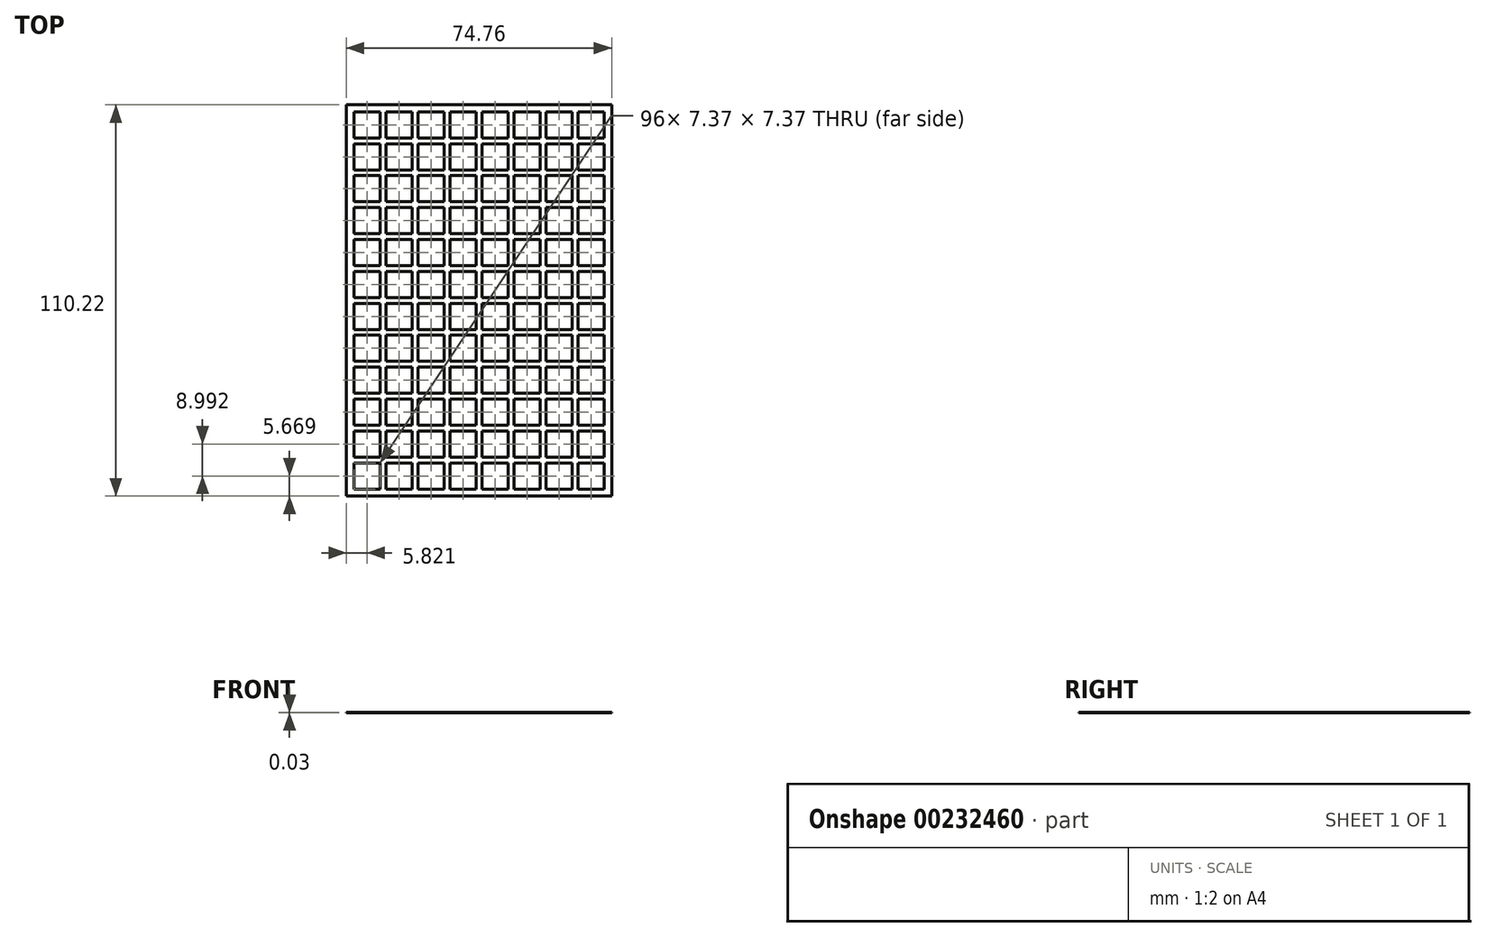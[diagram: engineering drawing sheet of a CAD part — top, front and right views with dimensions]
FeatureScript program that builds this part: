
annotation { "Feature Type Name" : "Feature", "Feature Type Description" : "" }
export const myFeature = defineFeature(function(context is Context, id is Id, definition is map)
    precondition{}
    {
        {
            var Q0;
            Q0=qCreatedBy(makeId("Top.planeOp"),FACE);
            var sketch = newSketch(context, id + "F0", { "sketchPlane" : qUnion([Q0])});
            skLineSegment(sketch, "E0.bottom", {"start": v(-37.38, 55.1) * mm, "end": v(37.38, 55.1) * mm});
            skLineSegment(sketch, "E0.top", {"start": v(-37.38, -55.1) * mm, "end": v(37.38, -55.1) * mm});
            skLineSegment(sketch, "E0.left", {"start": v(-37.38, 55.1) * mm, "end": v(-37.38, -55.1) * mm});
            skLineSegment(sketch, "E0.right", {"start": v(37.38, 55.1) * mm, "end": v(37.38, -55.1) * mm});
            skLineSegment(sketch, "E1.bottom", {"start": v(-35.24, 53.15) * mm, "end": v(-27.88, 53.15) * mm});
            skLineSegment(sketch, "E1.top", {"start": v(-35.24, 45.78) * mm, "end": v(-27.88, 45.78) * mm});
            skLineSegment(sketch, "E1.left", {"start": v(-35.24, 53.15) * mm, "end": v(-35.24, 45.78) * mm});
            skLineSegment(sketch, "E1.right", {"start": v(-27.88, 53.15) * mm, "end": v(-27.88, 45.78) * mm});
            skLineSegment(sketch, "E2.1.0.0", {"start": v(-18.86, 53.15) * mm, "end": v(-18.86, 45.78) * mm});
            skLineSegment(sketch, "E2.1.0.1", {"start": v(-26.23, 45.78) * mm, "end": v(-18.86, 45.78) * mm});
            skLineSegment(sketch, "E2.1.0.2", {"start": v(-26.23, 53.15) * mm, "end": v(-26.23, 45.78) * mm});
            skLineSegment(sketch, "E2.1.0.3", {"start": v(-26.23, 53.15) * mm, "end": v(-18.86, 53.15) * mm});
            skLineSegment(sketch, "E2.2.0.0", {"start": v(-9.84, 53.15) * mm, "end": v(-9.84, 45.78) * mm});
            skLineSegment(sketch, "E2.2.0.1", {"start": v(-17.2, 45.78) * mm, "end": v(-9.84, 45.78) * mm});
            skLineSegment(sketch, "E2.2.0.2", {"start": v(-17.2, 53.15) * mm, "end": v(-17.2, 45.78) * mm});
            skLineSegment(sketch, "E2.2.0.3", {"start": v(-17.2, 53.15) * mm, "end": v(-9.84, 53.15) * mm});
            skLineSegment(sketch, "E3.1.0.0", {"start": v(0.83, 53.15) * mm, "end": v(0.83, 45.78) * mm});
            skLineSegment(sketch, "E3.1.0.1", {"start": v(0.83, 45.78) * mm, "end": v(8.2, 45.78) * mm});
            skLineSegment(sketch, "E3.1.0.2", {"start": v(-0.83, 53.15) * mm, "end": v(-0.83, 45.78) * mm});
            skLineSegment(sketch, "E3.1.0.3", {"start": v(0.83, 53.15) * mm, "end": v(8.2, 53.15) * mm});
            skLineSegment(sketch, "E3.1.0.4", {"start": v(17.2, 53.15) * mm, "end": v(17.2, 45.78) * mm});
            skLineSegment(sketch, "E3.1.0.5", {"start": v(-8.2, 53.15) * mm, "end": v(-8.2, 45.78) * mm});
            skLineSegment(sketch, "E3.1.0.6", {"start": v(-8.2, 45.78) * mm, "end": v(-0.83, 45.78) * mm});
            skLineSegment(sketch, "E3.1.0.7", {"start": v(9.84, 53.15) * mm, "end": v(17.2, 53.15) * mm});
            skLineSegment(sketch, "E3.1.0.8", {"start": v(9.84, 45.78) * mm, "end": v(17.2, 45.78) * mm});
            skLineSegment(sketch, "E3.1.0.9", {"start": v(8.2, 53.15) * mm, "end": v(8.2, 45.78) * mm});
            skLineSegment(sketch, "E3.1.0.10", {"start": v(-8.2, 53.15) * mm, "end": v(-0.83, 53.15) * mm});
            skLineSegment(sketch, "E3.1.0.11", {"start": v(9.84, 53.15) * mm, "end": v(9.84, 45.78) * mm});
            skLineSegment(sketch, "E3.2.0.0", {"start": v(27.88, 53.15) * mm, "end": v(27.88, 45.78) * mm});
            skLineSegment(sketch, "E3.2.0.1", {"start": v(27.88, 45.78) * mm, "end": v(35.24, 45.78) * mm});
            skLineSegment(sketch, "E3.2.0.2", {"start": v(26.23, 53.15) * mm, "end": v(26.23, 45.78) * mm});
            skLineSegment(sketch, "E3.2.0.3", {"start": v(27.88, 53.15) * mm, "end": v(35.24, 53.15) * mm});
            skLineSegment(sketch, "E3.2.0.5", {"start": v(18.86, 53.15) * mm, "end": v(18.86, 45.78) * mm});
            skLineSegment(sketch, "E3.2.0.6", {"start": v(18.86, 45.78) * mm, "end": v(26.23, 45.78) * mm});
            skLineSegment(sketch, "E3.2.0.9", {"start": v(35.24, 53.15) * mm, "end": v(35.24, 45.78) * mm});
            skLineSegment(sketch, "E3.2.0.10", {"start": v(18.86, 53.15) * mm, "end": v(26.23, 53.15) * mm});
            skLineSegment(sketch, "E4.1.0.0", {"start": v(-8.2, 44.16) * mm, "end": v(-0.83, 44.16) * mm});
            skLineSegment(sketch, "E4.1.0.1", {"start": v(0.83, 44.16) * mm, "end": v(8.2, 44.16) * mm});
            skLineSegment(sketch, "E4.1.0.2", {"start": v(18.86, 44.16) * mm, "end": v(26.23, 44.16) * mm});
            skLineSegment(sketch, "E4.1.0.3", {"start": v(-17.2, 36.8) * mm, "end": v(-9.84, 36.8) * mm});
            skLineSegment(sketch, "E4.1.0.4", {"start": v(8.2, 44.16) * mm, "end": v(8.2, 36.8) * mm});
            skLineSegment(sketch, "E4.1.0.5", {"start": v(-35.24, 36.8) * mm, "end": v(-27.88, 36.8) * mm});
            skLineSegment(sketch, "E4.1.0.6", {"start": v(-17.2, 44.16) * mm, "end": v(-17.2, 36.8) * mm});
            skLineSegment(sketch, "E4.1.0.7", {"start": v(-17.2, 44.16) * mm, "end": v(-9.84, 44.16) * mm});
            skLineSegment(sketch, "E4.1.0.8", {"start": v(-0.83, 44.16) * mm, "end": v(-0.83, 36.8) * mm});
            skLineSegment(sketch, "E4.1.0.9", {"start": v(-35.24, 44.16) * mm, "end": v(-27.88, 44.16) * mm});
            skLineSegment(sketch, "E4.1.0.10", {"start": v(27.88, 44.16) * mm, "end": v(35.24, 44.16) * mm});
            skLineSegment(sketch, "E4.1.0.11", {"start": v(-8.2, 36.8) * mm, "end": v(-0.83, 36.8) * mm});
            skLineSegment(sketch, "E4.1.0.12", {"start": v(-35.24, 44.16) * mm, "end": v(-35.24, 36.8) * mm});
            skLineSegment(sketch, "E4.1.0.13", {"start": v(-27.88, 44.16) * mm, "end": v(-27.88, 36.8) * mm});
            skLineSegment(sketch, "E4.1.0.14", {"start": v(0.83, 36.8) * mm, "end": v(8.2, 36.8) * mm});
            skLineSegment(sketch, "E4.1.0.15", {"start": v(18.86, 36.8) * mm, "end": v(26.23, 36.8) * mm});
            skLineSegment(sketch, "E4.1.0.16", {"start": v(-18.86, 44.16) * mm, "end": v(-18.86, 36.8) * mm});
            skLineSegment(sketch, "E4.1.0.17", {"start": v(-26.23, 36.8) * mm, "end": v(-18.86, 36.8) * mm});
            skLineSegment(sketch, "E4.1.0.18", {"start": v(-26.23, 44.16) * mm, "end": v(-26.23, 36.8) * mm});
            skLineSegment(sketch, "E4.1.0.19", {"start": v(-26.23, 44.16) * mm, "end": v(-18.86, 44.16) * mm});
            skLineSegment(sketch, "E4.1.0.20", {"start": v(-9.84, 44.16) * mm, "end": v(-9.84, 36.8) * mm});
            skLineSegment(sketch, "E4.1.0.21", {"start": v(9.84, 44.16) * mm, "end": v(9.84, 36.8) * mm});
            skLineSegment(sketch, "E4.1.0.22", {"start": v(9.84, 44.16) * mm, "end": v(17.2, 44.16) * mm});
            skLineSegment(sketch, "E4.1.0.23", {"start": v(17.2, 44.16) * mm, "end": v(17.2, 36.8) * mm});
            skLineSegment(sketch, "E4.1.0.24", {"start": v(27.88, 36.8) * mm, "end": v(35.24, 36.8) * mm});
            skLineSegment(sketch, "E4.1.0.25", {"start": v(0.83, 44.16) * mm, "end": v(0.83, 36.8) * mm});
            skLineSegment(sketch, "E4.1.0.26", {"start": v(18.86, 44.16) * mm, "end": v(18.86, 36.8) * mm});
            skLineSegment(sketch, "E4.1.0.27", {"start": v(27.88, 44.16) * mm, "end": v(27.88, 36.8) * mm});
            skLineSegment(sketch, "E4.1.0.28", {"start": v(9.84, 36.8) * mm, "end": v(17.2, 36.8) * mm});
            skLineSegment(sketch, "E4.1.0.29", {"start": v(26.23, 44.16) * mm, "end": v(26.23, 36.8) * mm});
            skLineSegment(sketch, "E4.1.0.30", {"start": v(-8.2, 44.16) * mm, "end": v(-8.2, 36.8) * mm});
            skLineSegment(sketch, "E4.1.0.31", {"start": v(35.24, 44.16) * mm, "end": v(35.24, 36.8) * mm});
            skLineSegment(sketch, "E4.2.0.0", {"start": v(-8.2, 35.17) * mm, "end": v(-0.83, 35.17) * mm});
            skLineSegment(sketch, "E4.2.0.1", {"start": v(0.83, 35.17) * mm, "end": v(8.2, 35.17) * mm});
            skLineSegment(sketch, "E4.2.0.2", {"start": v(18.86, 35.17) * mm, "end": v(26.23, 35.17) * mm});
            skLineSegment(sketch, "E4.2.0.3", {"start": v(-17.2, 27.8) * mm, "end": v(-9.84, 27.8) * mm});
            skLineSegment(sketch, "E4.2.0.4", {"start": v(8.2, 35.17) * mm, "end": v(8.2, 27.8) * mm});
            skLineSegment(sketch, "E4.2.0.5", {"start": v(-35.24, 27.8) * mm, "end": v(-27.88, 27.8) * mm});
            skLineSegment(sketch, "E4.2.0.6", {"start": v(-17.2, 35.17) * mm, "end": v(-17.2, 27.8) * mm});
            skLineSegment(sketch, "E4.2.0.7", {"start": v(-17.2, 35.17) * mm, "end": v(-9.84, 35.17) * mm});
            skLineSegment(sketch, "E4.2.0.8", {"start": v(-0.83, 35.17) * mm, "end": v(-0.83, 27.8) * mm});
            skLineSegment(sketch, "E4.2.0.9", {"start": v(-35.24, 35.17) * mm, "end": v(-27.88, 35.17) * mm});
            skLineSegment(sketch, "E4.2.0.10", {"start": v(27.88, 35.17) * mm, "end": v(35.24, 35.17) * mm});
            skLineSegment(sketch, "E4.2.0.11", {"start": v(-8.2, 27.8) * mm, "end": v(-0.83, 27.8) * mm});
            skLineSegment(sketch, "E4.2.0.12", {"start": v(-35.24, 35.17) * mm, "end": v(-35.24, 27.8) * mm});
            skLineSegment(sketch, "E4.2.0.13", {"start": v(-27.88, 35.17) * mm, "end": v(-27.88, 27.8) * mm});
            skLineSegment(sketch, "E4.2.0.14", {"start": v(0.83, 27.8) * mm, "end": v(8.2, 27.8) * mm});
            skLineSegment(sketch, "E4.2.0.15", {"start": v(18.86, 27.8) * mm, "end": v(26.23, 27.8) * mm});
            skLineSegment(sketch, "E4.2.0.16", {"start": v(-18.86, 35.17) * mm, "end": v(-18.86, 27.8) * mm});
            skLineSegment(sketch, "E4.2.0.17", {"start": v(-26.23, 27.8) * mm, "end": v(-18.86, 27.8) * mm});
            skLineSegment(sketch, "E4.2.0.18", {"start": v(-26.23, 35.17) * mm, "end": v(-26.23, 27.8) * mm});
            skLineSegment(sketch, "E4.2.0.19", {"start": v(-26.23, 35.17) * mm, "end": v(-18.86, 35.17) * mm});
            skLineSegment(sketch, "E4.2.0.20", {"start": v(-9.84, 35.17) * mm, "end": v(-9.84, 27.8) * mm});
            skLineSegment(sketch, "E4.2.0.21", {"start": v(9.84, 35.17) * mm, "end": v(9.84, 27.8) * mm});
            skLineSegment(sketch, "E4.2.0.22", {"start": v(9.84, 35.17) * mm, "end": v(17.2, 35.17) * mm});
            skLineSegment(sketch, "E4.2.0.23", {"start": v(17.2, 35.17) * mm, "end": v(17.2, 27.8) * mm});
            skLineSegment(sketch, "E4.2.0.24", {"start": v(27.88, 27.8) * mm, "end": v(35.24, 27.8) * mm});
            skLineSegment(sketch, "E4.2.0.25", {"start": v(0.83, 35.17) * mm, "end": v(0.83, 27.8) * mm});
            skLineSegment(sketch, "E4.2.0.26", {"start": v(18.86, 35.17) * mm, "end": v(18.86, 27.8) * mm});
            skLineSegment(sketch, "E4.2.0.27", {"start": v(27.88, 35.17) * mm, "end": v(27.88, 27.8) * mm});
            skLineSegment(sketch, "E4.2.0.28", {"start": v(9.84, 27.8) * mm, "end": v(17.2, 27.8) * mm});
            skLineSegment(sketch, "E4.2.0.29", {"start": v(26.23, 35.17) * mm, "end": v(26.23, 27.8) * mm});
            skLineSegment(sketch, "E4.2.0.30", {"start": v(-8.2, 35.17) * mm, "end": v(-8.2, 27.8) * mm});
            skLineSegment(sketch, "E4.2.0.31", {"start": v(35.24, 35.17) * mm, "end": v(35.24, 27.8) * mm});
            skLineSegment(sketch, "E4.direction1", {"start": v(-35.24, 45.78) * mm, "end": v(-35.24, 36.8) * mm, "construction": true});
            skLineSegment(sketch, "E5.0.3.0", {"start": v(-8.2, 26.17) * mm, "end": v(-0.83, 26.17) * mm});
            skLineSegment(sketch, "E5.3.3.0", {"start": v(0.83, 26.17) * mm, "end": v(8.2, 26.17) * mm});
            skLineSegment(sketch, "E5.6.3.0", {"start": v(18.86, 26.17) * mm, "end": v(26.23, 26.17) * mm});
            skLineSegment(sketch, "E5.9.3.0", {"start": v(-17.2, 18.8) * mm, "end": v(-9.84, 18.8) * mm});
            skLineSegment(sketch, "E5.12.3.0", {"start": v(8.2, 26.17) * mm, "end": v(8.2, 18.8) * mm});
            skLineSegment(sketch, "E5.15.3.0", {"start": v(-35.24, 18.8) * mm, "end": v(-27.88, 18.8) * mm});
            skLineSegment(sketch, "E5.18.3.0", {"start": v(-17.2, 26.17) * mm, "end": v(-17.2, 18.8) * mm});
            skLineSegment(sketch, "E5.21.3.0", {"start": v(-17.2, 26.17) * mm, "end": v(-9.84, 26.17) * mm});
            skLineSegment(sketch, "E5.24.3.0", {"start": v(-0.83, 26.17) * mm, "end": v(-0.83, 18.8) * mm});
            skLineSegment(sketch, "E5.27.3.0", {"start": v(-35.24, 26.17) * mm, "end": v(-27.88, 26.17) * mm});
            skLineSegment(sketch, "E5.30.3.0", {"start": v(27.88, 26.17) * mm, "end": v(35.24, 26.17) * mm});
            skLineSegment(sketch, "E5.33.3.0", {"start": v(-8.2, 18.8) * mm, "end": v(-0.83, 18.8) * mm});
            skLineSegment(sketch, "E5.36.3.0", {"start": v(-35.24, 26.17) * mm, "end": v(-35.24, 18.8) * mm});
            skLineSegment(sketch, "E5.39.3.0", {"start": v(-27.88, 26.17) * mm, "end": v(-27.88, 18.8) * mm});
            skLineSegment(sketch, "E5.42.3.0", {"start": v(0.83, 18.8) * mm, "end": v(8.2, 18.8) * mm});
            skLineSegment(sketch, "E5.45.3.0", {"start": v(18.86, 18.8) * mm, "end": v(26.23, 18.8) * mm});
            skLineSegment(sketch, "E5.48.3.0", {"start": v(-18.86, 26.17) * mm, "end": v(-18.86, 18.8) * mm});
            skLineSegment(sketch, "E5.51.3.0", {"start": v(-26.23, 18.8) * mm, "end": v(-18.86, 18.8) * mm});
            skLineSegment(sketch, "E5.54.3.0", {"start": v(-26.23, 26.17) * mm, "end": v(-26.23, 18.8) * mm});
            skLineSegment(sketch, "E5.57.3.0", {"start": v(-26.23, 26.17) * mm, "end": v(-18.86, 26.17) * mm});
            skLineSegment(sketch, "E5.60.3.0", {"start": v(-9.84, 26.17) * mm, "end": v(-9.84, 18.8) * mm});
            skLineSegment(sketch, "E5.63.3.0", {"start": v(9.84, 26.17) * mm, "end": v(9.84, 18.8) * mm});
            skLineSegment(sketch, "E5.66.3.0", {"start": v(9.84, 26.17) * mm, "end": v(17.2, 26.17) * mm});
            skLineSegment(sketch, "E5.69.3.0", {"start": v(17.2, 26.17) * mm, "end": v(17.2, 18.8) * mm});
            skLineSegment(sketch, "E5.72.3.0", {"start": v(27.88, 18.8) * mm, "end": v(35.24, 18.8) * mm});
            skLineSegment(sketch, "E5.75.3.0", {"start": v(0.83, 26.17) * mm, "end": v(0.83, 18.8) * mm});
            skLineSegment(sketch, "E5.78.3.0", {"start": v(18.86, 26.17) * mm, "end": v(18.86, 18.8) * mm});
            skLineSegment(sketch, "E5.81.3.0", {"start": v(27.88, 26.17) * mm, "end": v(27.88, 18.8) * mm});
            skLineSegment(sketch, "E5.84.3.0", {"start": v(9.84, 18.8) * mm, "end": v(17.2, 18.8) * mm});
            skLineSegment(sketch, "E5.87.3.0", {"start": v(26.23, 26.17) * mm, "end": v(26.23, 18.8) * mm});
            skLineSegment(sketch, "E5.90.3.0", {"start": v(-8.2, 26.17) * mm, "end": v(-8.2, 18.8) * mm});
            skLineSegment(sketch, "E5.93.3.0", {"start": v(35.24, 26.17) * mm, "end": v(35.24, 18.8) * mm});
            skLineSegment(sketch, "E5.0.4.0", {"start": v(-8.2, 17.18) * mm, "end": v(-0.83, 17.18) * mm});
            skLineSegment(sketch, "E5.3.4.0", {"start": v(0.83, 17.18) * mm, "end": v(8.2, 17.18) * mm});
            skLineSegment(sketch, "E5.6.4.0", {"start": v(18.86, 17.18) * mm, "end": v(26.23, 17.18) * mm});
            skLineSegment(sketch, "E5.9.4.0", {"start": v(-17.2, 9.82) * mm, "end": v(-9.84, 9.82) * mm});
            skLineSegment(sketch, "E5.12.4.0", {"start": v(8.2, 17.18) * mm, "end": v(8.2, 9.82) * mm});
            skLineSegment(sketch, "E5.15.4.0", {"start": v(-35.24, 9.82) * mm, "end": v(-27.88, 9.82) * mm});
            skLineSegment(sketch, "E5.18.4.0", {"start": v(-17.2, 17.18) * mm, "end": v(-17.2, 9.82) * mm});
            skLineSegment(sketch, "E5.21.4.0", {"start": v(-17.2, 17.18) * mm, "end": v(-9.84, 17.18) * mm});
            skLineSegment(sketch, "E5.24.4.0", {"start": v(-0.83, 17.18) * mm, "end": v(-0.83, 9.82) * mm});
            skLineSegment(sketch, "E5.27.4.0", {"start": v(-35.24, 17.18) * mm, "end": v(-27.88, 17.18) * mm});
            skLineSegment(sketch, "E5.30.4.0", {"start": v(27.88, 17.18) * mm, "end": v(35.24, 17.18) * mm});
            skLineSegment(sketch, "E5.33.4.0", {"start": v(-8.2, 9.82) * mm, "end": v(-0.83, 9.82) * mm});
            skLineSegment(sketch, "E5.36.4.0", {"start": v(-35.24, 17.18) * mm, "end": v(-35.24, 9.82) * mm});
            skLineSegment(sketch, "E5.39.4.0", {"start": v(-27.88, 17.18) * mm, "end": v(-27.88, 9.82) * mm});
            skLineSegment(sketch, "E5.42.4.0", {"start": v(0.83, 9.82) * mm, "end": v(8.2, 9.82) * mm});
            skLineSegment(sketch, "E5.45.4.0", {"start": v(18.86, 9.82) * mm, "end": v(26.23, 9.82) * mm});
            skLineSegment(sketch, "E5.48.4.0", {"start": v(-18.86, 17.18) * mm, "end": v(-18.86, 9.82) * mm});
            skLineSegment(sketch, "E5.51.4.0", {"start": v(-26.23, 9.82) * mm, "end": v(-18.86, 9.82) * mm});
            skLineSegment(sketch, "E5.54.4.0", {"start": v(-26.23, 17.18) * mm, "end": v(-26.23, 9.82) * mm});
            skLineSegment(sketch, "E5.57.4.0", {"start": v(-26.23, 17.18) * mm, "end": v(-18.86, 17.18) * mm});
            skLineSegment(sketch, "E5.60.4.0", {"start": v(-9.84, 17.18) * mm, "end": v(-9.84, 9.82) * mm});
            skLineSegment(sketch, "E5.63.4.0", {"start": v(9.84, 17.18) * mm, "end": v(9.84, 9.82) * mm});
            skLineSegment(sketch, "E5.66.4.0", {"start": v(9.84, 17.18) * mm, "end": v(17.2, 17.18) * mm});
            skLineSegment(sketch, "E5.69.4.0", {"start": v(17.2, 17.18) * mm, "end": v(17.2, 9.82) * mm});
            skLineSegment(sketch, "E5.72.4.0", {"start": v(27.88, 9.82) * mm, "end": v(35.24, 9.82) * mm});
            skLineSegment(sketch, "E5.75.4.0", {"start": v(0.83, 17.18) * mm, "end": v(0.83, 9.82) * mm});
            skLineSegment(sketch, "E5.78.4.0", {"start": v(18.86, 17.18) * mm, "end": v(18.86, 9.82) * mm});
            skLineSegment(sketch, "E5.81.4.0", {"start": v(27.88, 17.18) * mm, "end": v(27.88, 9.82) * mm});
            skLineSegment(sketch, "E5.84.4.0", {"start": v(9.84, 9.82) * mm, "end": v(17.2, 9.82) * mm});
            skLineSegment(sketch, "E5.87.4.0", {"start": v(26.23, 17.18) * mm, "end": v(26.23, 9.82) * mm});
            skLineSegment(sketch, "E5.90.4.0", {"start": v(-8.2, 17.18) * mm, "end": v(-8.2, 9.82) * mm});
            skLineSegment(sketch, "E5.93.4.0", {"start": v(35.24, 17.18) * mm, "end": v(35.24, 9.82) * mm});
            skLineSegment(sketch, "E5.0.5.0", {"start": v(-8.2, 8.2) * mm, "end": v(-0.83, 8.2) * mm});
            skLineSegment(sketch, "E5.3.5.0", {"start": v(0.83, 8.2) * mm, "end": v(8.2, 8.2) * mm});
            skLineSegment(sketch, "E5.6.5.0", {"start": v(18.86, 8.2) * mm, "end": v(26.23, 8.2) * mm});
            skLineSegment(sketch, "E5.9.5.0", {"start": v(-17.2, 0.83) * mm, "end": v(-9.84, 0.83) * mm});
            skLineSegment(sketch, "E5.12.5.0", {"start": v(8.2, 8.2) * mm, "end": v(8.2, 0.83) * mm});
            skLineSegment(sketch, "E5.15.5.0", {"start": v(-35.24, 0.83) * mm, "end": v(-27.88, 0.83) * mm});
            skLineSegment(sketch, "E5.18.5.0", {"start": v(-17.2, 8.2) * mm, "end": v(-17.2, 0.83) * mm});
            skLineSegment(sketch, "E5.21.5.0", {"start": v(-17.2, 8.2) * mm, "end": v(-9.84, 8.2) * mm});
            skLineSegment(sketch, "E5.24.5.0", {"start": v(-0.83, 8.2) * mm, "end": v(-0.83, 0.83) * mm});
            skLineSegment(sketch, "E5.27.5.0", {"start": v(-35.24, 8.2) * mm, "end": v(-27.88, 8.2) * mm});
            skLineSegment(sketch, "E5.30.5.0", {"start": v(27.88, 8.2) * mm, "end": v(35.24, 8.2) * mm});
            skLineSegment(sketch, "E5.33.5.0", {"start": v(-8.2, 0.83) * mm, "end": v(-0.83, 0.83) * mm});
            skLineSegment(sketch, "E5.36.5.0", {"start": v(-35.24, 8.2) * mm, "end": v(-35.24, 0.83) * mm});
            skLineSegment(sketch, "E5.39.5.0", {"start": v(-27.88, 8.2) * mm, "end": v(-27.88, 0.83) * mm});
            skLineSegment(sketch, "E5.42.5.0", {"start": v(0.83, 0.83) * mm, "end": v(8.2, 0.83) * mm});
            skLineSegment(sketch, "E5.45.5.0", {"start": v(18.86, 0.83) * mm, "end": v(26.23, 0.83) * mm});
            skLineSegment(sketch, "E5.48.5.0", {"start": v(-18.86, 8.2) * mm, "end": v(-18.86, 0.83) * mm});
            skLineSegment(sketch, "E5.51.5.0", {"start": v(-26.23, 0.83) * mm, "end": v(-18.86, 0.83) * mm});
            skLineSegment(sketch, "E5.54.5.0", {"start": v(-26.23, 8.2) * mm, "end": v(-26.23, 0.83) * mm});
            skLineSegment(sketch, "E5.57.5.0", {"start": v(-26.23, 8.2) * mm, "end": v(-18.86, 8.2) * mm});
            skLineSegment(sketch, "E5.60.5.0", {"start": v(-9.84, 8.2) * mm, "end": v(-9.84, 0.83) * mm});
            skLineSegment(sketch, "E5.63.5.0", {"start": v(9.84, 8.2) * mm, "end": v(9.84, 0.83) * mm});
            skLineSegment(sketch, "E5.66.5.0", {"start": v(9.84, 8.2) * mm, "end": v(17.2, 8.2) * mm});
            skLineSegment(sketch, "E5.69.5.0", {"start": v(17.2, 8.2) * mm, "end": v(17.2, 0.83) * mm});
            skLineSegment(sketch, "E5.72.5.0", {"start": v(27.88, 0.83) * mm, "end": v(35.24, 0.83) * mm});
            skLineSegment(sketch, "E5.75.5.0", {"start": v(0.83, 8.2) * mm, "end": v(0.83, 0.83) * mm});
            skLineSegment(sketch, "E5.78.5.0", {"start": v(18.86, 8.2) * mm, "end": v(18.86, 0.83) * mm});
            skLineSegment(sketch, "E5.81.5.0", {"start": v(27.88, 8.2) * mm, "end": v(27.88, 0.83) * mm});
            skLineSegment(sketch, "E5.84.5.0", {"start": v(9.84, 0.83) * mm, "end": v(17.2, 0.83) * mm});
            skLineSegment(sketch, "E5.87.5.0", {"start": v(26.23, 8.2) * mm, "end": v(26.23, 0.83) * mm});
            skLineSegment(sketch, "E5.90.5.0", {"start": v(-8.2, 8.2) * mm, "end": v(-8.2, 0.83) * mm});
            skLineSegment(sketch, "E5.93.5.0", {"start": v(35.24, 8.2) * mm, "end": v(35.24, 0.83) * mm});
            skLineSegment(sketch, "E5.0.6.0", {"start": v(-8.2, -0.8) * mm, "end": v(-0.83, -0.8) * mm});
            skLineSegment(sketch, "E5.3.6.0", {"start": v(0.83, -0.8) * mm, "end": v(8.2, -0.8) * mm});
            skLineSegment(sketch, "E5.6.6.0", {"start": v(18.86, -0.8) * mm, "end": v(26.23, -0.8) * mm});
            skLineSegment(sketch, "E5.9.6.0", {"start": v(-17.2, -8.17) * mm, "end": v(-9.84, -8.17) * mm});
            skLineSegment(sketch, "E5.12.6.0", {"start": v(8.2, -0.8) * mm, "end": v(8.2, -8.17) * mm});
            skLineSegment(sketch, "E5.15.6.0", {"start": v(-35.24, -8.17) * mm, "end": v(-27.88, -8.17) * mm});
            skLineSegment(sketch, "E5.18.6.0", {"start": v(-17.2, -0.8) * mm, "end": v(-17.2, -8.17) * mm});
            skLineSegment(sketch, "E5.21.6.0", {"start": v(-17.2, -0.8) * mm, "end": v(-9.84, -0.8) * mm});
            skLineSegment(sketch, "E5.24.6.0", {"start": v(-0.83, -0.8) * mm, "end": v(-0.83, -8.17) * mm});
            skLineSegment(sketch, "E5.27.6.0", {"start": v(-35.24, -0.8) * mm, "end": v(-27.88, -0.8) * mm});
            skLineSegment(sketch, "E5.30.6.0", {"start": v(27.88, -0.8) * mm, "end": v(35.24, -0.8) * mm});
            skLineSegment(sketch, "E5.33.6.0", {"start": v(-8.2, -8.17) * mm, "end": v(-0.83, -8.17) * mm});
            skLineSegment(sketch, "E5.36.6.0", {"start": v(-35.24, -0.8) * mm, "end": v(-35.24, -8.17) * mm});
            skLineSegment(sketch, "E5.39.6.0", {"start": v(-27.88, -0.8) * mm, "end": v(-27.88, -8.17) * mm});
            skLineSegment(sketch, "E5.42.6.0", {"start": v(0.83, -8.17) * mm, "end": v(8.2, -8.17) * mm});
            skLineSegment(sketch, "E5.45.6.0", {"start": v(18.86, -8.17) * mm, "end": v(26.23, -8.17) * mm});
            skLineSegment(sketch, "E5.48.6.0", {"start": v(-18.86, -0.8) * mm, "end": v(-18.86, -8.17) * mm});
            skLineSegment(sketch, "E5.51.6.0", {"start": v(-26.23, -8.17) * mm, "end": v(-18.86, -8.17) * mm});
            skLineSegment(sketch, "E5.54.6.0", {"start": v(-26.23, -0.8) * mm, "end": v(-26.23, -8.17) * mm});
            skLineSegment(sketch, "E5.57.6.0", {"start": v(-26.23, -0.8) * mm, "end": v(-18.86, -0.8) * mm});
            skLineSegment(sketch, "E5.60.6.0", {"start": v(-9.84, -0.8) * mm, "end": v(-9.84, -8.17) * mm});
            skLineSegment(sketch, "E5.63.6.0", {"start": v(9.84, -0.8) * mm, "end": v(9.84, -8.17) * mm});
            skLineSegment(sketch, "E5.66.6.0", {"start": v(9.84, -0.8) * mm, "end": v(17.2, -0.8) * mm});
            skLineSegment(sketch, "E5.69.6.0", {"start": v(17.2, -0.8) * mm, "end": v(17.2, -8.17) * mm});
            skLineSegment(sketch, "E5.72.6.0", {"start": v(27.88, -8.17) * mm, "end": v(35.24, -8.17) * mm});
            skLineSegment(sketch, "E5.75.6.0", {"start": v(0.83, -0.8) * mm, "end": v(0.83, -8.17) * mm});
            skLineSegment(sketch, "E5.78.6.0", {"start": v(18.86, -0.8) * mm, "end": v(18.86, -8.17) * mm});
            skLineSegment(sketch, "E5.81.6.0", {"start": v(27.88, -0.8) * mm, "end": v(27.88, -8.17) * mm});
            skLineSegment(sketch, "E5.84.6.0", {"start": v(9.84, -8.17) * mm, "end": v(17.2, -8.17) * mm});
            skLineSegment(sketch, "E5.87.6.0", {"start": v(26.23, -0.8) * mm, "end": v(26.23, -8.17) * mm});
            skLineSegment(sketch, "E5.90.6.0", {"start": v(-8.2, -0.8) * mm, "end": v(-8.2, -8.17) * mm});
            skLineSegment(sketch, "E5.93.6.0", {"start": v(35.24, -0.8) * mm, "end": v(35.24, -8.17) * mm});
            skLineSegment(sketch, "E5.0.7.0", {"start": v(-8.2, -9.8) * mm, "end": v(-0.83, -9.8) * mm});
            skLineSegment(sketch, "E5.3.7.0", {"start": v(0.83, -9.8) * mm, "end": v(8.2, -9.8) * mm});
            skLineSegment(sketch, "E5.6.7.0", {"start": v(18.86, -9.8) * mm, "end": v(26.23, -9.8) * mm});
            skLineSegment(sketch, "E5.9.7.0", {"start": v(-17.2, -17.16) * mm, "end": v(-9.84, -17.16) * mm});
            skLineSegment(sketch, "E5.12.7.0", {"start": v(8.2, -9.8) * mm, "end": v(8.2, -17.16) * mm});
            skLineSegment(sketch, "E5.15.7.0", {"start": v(-35.24, -17.16) * mm, "end": v(-27.88, -17.16) * mm});
            skLineSegment(sketch, "E5.18.7.0", {"start": v(-17.2, -9.8) * mm, "end": v(-17.2, -17.16) * mm});
            skLineSegment(sketch, "E5.21.7.0", {"start": v(-17.2, -9.8) * mm, "end": v(-9.84, -9.8) * mm});
            skLineSegment(sketch, "E5.24.7.0", {"start": v(-0.83, -9.8) * mm, "end": v(-0.83, -17.16) * mm});
            skLineSegment(sketch, "E5.27.7.0", {"start": v(-35.24, -9.8) * mm, "end": v(-27.88, -9.8) * mm});
            skLineSegment(sketch, "E5.30.7.0", {"start": v(27.88, -9.8) * mm, "end": v(35.24, -9.8) * mm});
            skLineSegment(sketch, "E5.33.7.0", {"start": v(-8.2, -17.16) * mm, "end": v(-0.83, -17.16) * mm});
            skLineSegment(sketch, "E5.36.7.0", {"start": v(-35.24, -9.8) * mm, "end": v(-35.24, -17.16) * mm});
            skLineSegment(sketch, "E5.39.7.0", {"start": v(-27.88, -9.8) * mm, "end": v(-27.88, -17.16) * mm});
            skLineSegment(sketch, "E5.42.7.0", {"start": v(0.83, -17.16) * mm, "end": v(8.2, -17.16) * mm});
            skLineSegment(sketch, "E5.45.7.0", {"start": v(18.86, -17.16) * mm, "end": v(26.23, -17.16) * mm});
            skLineSegment(sketch, "E5.48.7.0", {"start": v(-18.86, -9.8) * mm, "end": v(-18.86, -17.16) * mm});
            skLineSegment(sketch, "E5.51.7.0", {"start": v(-26.23, -17.16) * mm, "end": v(-18.86, -17.16) * mm});
            skLineSegment(sketch, "E5.54.7.0", {"start": v(-26.23, -9.8) * mm, "end": v(-26.23, -17.16) * mm});
            skLineSegment(sketch, "E5.57.7.0", {"start": v(-26.23, -9.8) * mm, "end": v(-18.86, -9.8) * mm});
            skLineSegment(sketch, "E5.60.7.0", {"start": v(-9.84, -9.8) * mm, "end": v(-9.84, -17.16) * mm});
            skLineSegment(sketch, "E5.63.7.0", {"start": v(9.84, -9.8) * mm, "end": v(9.84, -17.16) * mm});
            skLineSegment(sketch, "E5.66.7.0", {"start": v(9.84, -9.8) * mm, "end": v(17.2, -9.8) * mm});
            skLineSegment(sketch, "E5.69.7.0", {"start": v(17.2, -9.8) * mm, "end": v(17.2, -17.16) * mm});
            skLineSegment(sketch, "E5.72.7.0", {"start": v(27.88, -17.16) * mm, "end": v(35.24, -17.16) * mm});
            skLineSegment(sketch, "E5.75.7.0", {"start": v(0.83, -9.8) * mm, "end": v(0.83, -17.16) * mm});
            skLineSegment(sketch, "E5.78.7.0", {"start": v(18.86, -9.8) * mm, "end": v(18.86, -17.16) * mm});
            skLineSegment(sketch, "E5.81.7.0", {"start": v(27.88, -9.8) * mm, "end": v(27.88, -17.16) * mm});
            skLineSegment(sketch, "E5.84.7.0", {"start": v(9.84, -17.16) * mm, "end": v(17.2, -17.16) * mm});
            skLineSegment(sketch, "E5.87.7.0", {"start": v(26.23, -9.8) * mm, "end": v(26.23, -17.16) * mm});
            skLineSegment(sketch, "E5.90.7.0", {"start": v(-8.2, -9.8) * mm, "end": v(-8.2, -17.16) * mm});
            skLineSegment(sketch, "E5.93.7.0", {"start": v(35.24, -9.8) * mm, "end": v(35.24, -17.16) * mm});
            skLineSegment(sketch, "E5.0.8.0", {"start": v(-8.2, -18.78) * mm, "end": v(-0.83, -18.78) * mm});
            skLineSegment(sketch, "E5.3.8.0", {"start": v(0.83, -18.78) * mm, "end": v(8.2, -18.78) * mm});
            skLineSegment(sketch, "E5.6.8.0", {"start": v(18.86, -18.78) * mm, "end": v(26.23, -18.78) * mm});
            skLineSegment(sketch, "E5.9.8.0", {"start": v(-17.2, -26.15) * mm, "end": v(-9.84, -26.15) * mm});
            skLineSegment(sketch, "E5.12.8.0", {"start": v(8.2, -18.78) * mm, "end": v(8.2, -26.15) * mm});
            skLineSegment(sketch, "E5.15.8.0", {"start": v(-35.24, -26.15) * mm, "end": v(-27.88, -26.15) * mm});
            skLineSegment(sketch, "E5.18.8.0", {"start": v(-17.2, -18.78) * mm, "end": v(-17.2, -26.15) * mm});
            skLineSegment(sketch, "E5.21.8.0", {"start": v(-17.2, -18.78) * mm, "end": v(-9.84, -18.78) * mm});
            skLineSegment(sketch, "E5.24.8.0", {"start": v(-0.83, -18.78) * mm, "end": v(-0.83, -26.15) * mm});
            skLineSegment(sketch, "E5.27.8.0", {"start": v(-35.24, -18.78) * mm, "end": v(-27.88, -18.78) * mm});
            skLineSegment(sketch, "E5.30.8.0", {"start": v(27.88, -18.78) * mm, "end": v(35.24, -18.78) * mm});
            skLineSegment(sketch, "E5.33.8.0", {"start": v(-8.2, -26.15) * mm, "end": v(-0.83, -26.15) * mm});
            skLineSegment(sketch, "E5.36.8.0", {"start": v(-35.24, -18.78) * mm, "end": v(-35.24, -26.15) * mm});
            skLineSegment(sketch, "E5.39.8.0", {"start": v(-27.88, -18.78) * mm, "end": v(-27.88, -26.15) * mm});
            skLineSegment(sketch, "E5.42.8.0", {"start": v(0.83, -26.15) * mm, "end": v(8.2, -26.15) * mm});
            skLineSegment(sketch, "E5.45.8.0", {"start": v(18.86, -26.15) * mm, "end": v(26.23, -26.15) * mm});
            skLineSegment(sketch, "E5.48.8.0", {"start": v(-18.86, -18.78) * mm, "end": v(-18.86, -26.15) * mm});
            skLineSegment(sketch, "E5.51.8.0", {"start": v(-26.23, -26.15) * mm, "end": v(-18.86, -26.15) * mm});
            skLineSegment(sketch, "E5.54.8.0", {"start": v(-26.23, -18.78) * mm, "end": v(-26.23, -26.15) * mm});
            skLineSegment(sketch, "E5.57.8.0", {"start": v(-26.23, -18.78) * mm, "end": v(-18.86, -18.78) * mm});
            skLineSegment(sketch, "E5.60.8.0", {"start": v(-9.84, -18.78) * mm, "end": v(-9.84, -26.15) * mm});
            skLineSegment(sketch, "E5.63.8.0", {"start": v(9.84, -18.78) * mm, "end": v(9.84, -26.15) * mm});
            skLineSegment(sketch, "E5.66.8.0", {"start": v(9.84, -18.78) * mm, "end": v(17.2, -18.78) * mm});
            skLineSegment(sketch, "E5.69.8.0", {"start": v(17.2, -18.78) * mm, "end": v(17.2, -26.15) * mm});
            skLineSegment(sketch, "E5.72.8.0", {"start": v(27.88, -26.15) * mm, "end": v(35.24, -26.15) * mm});
            skLineSegment(sketch, "E5.75.8.0", {"start": v(0.83, -18.78) * mm, "end": v(0.83, -26.15) * mm});
            skLineSegment(sketch, "E5.78.8.0", {"start": v(18.86, -18.78) * mm, "end": v(18.86, -26.15) * mm});
            skLineSegment(sketch, "E5.81.8.0", {"start": v(27.88, -18.78) * mm, "end": v(27.88, -26.15) * mm});
            skLineSegment(sketch, "E5.84.8.0", {"start": v(9.84, -26.15) * mm, "end": v(17.2, -26.15) * mm});
            skLineSegment(sketch, "E5.87.8.0", {"start": v(26.23, -18.78) * mm, "end": v(26.23, -26.15) * mm});
            skLineSegment(sketch, "E5.90.8.0", {"start": v(-8.2, -18.78) * mm, "end": v(-8.2, -26.15) * mm});
            skLineSegment(sketch, "E5.93.8.0", {"start": v(35.24, -18.78) * mm, "end": v(35.24, -26.15) * mm});
            skLineSegment(sketch, "E5.0.9.0", {"start": v(-8.2, -27.77) * mm, "end": v(-0.83, -27.77) * mm});
            skLineSegment(sketch, "E5.3.9.0", {"start": v(0.83, -27.77) * mm, "end": v(8.2, -27.77) * mm});
            skLineSegment(sketch, "E5.6.9.0", {"start": v(18.86, -27.77) * mm, "end": v(26.23, -27.77) * mm});
            skLineSegment(sketch, "E5.9.9.0", {"start": v(-17.2, -35.14) * mm, "end": v(-9.84, -35.14) * mm});
            skLineSegment(sketch, "E5.12.9.0", {"start": v(8.2, -27.77) * mm, "end": v(8.2, -35.14) * mm});
            skLineSegment(sketch, "E5.15.9.0", {"start": v(-35.24, -35.14) * mm, "end": v(-27.88, -35.14) * mm});
            skLineSegment(sketch, "E5.18.9.0", {"start": v(-17.2, -27.77) * mm, "end": v(-17.2, -35.14) * mm});
            skLineSegment(sketch, "E5.21.9.0", {"start": v(-17.2, -27.77) * mm, "end": v(-9.84, -27.77) * mm});
            skLineSegment(sketch, "E5.24.9.0", {"start": v(-0.83, -27.77) * mm, "end": v(-0.83, -35.14) * mm});
            skLineSegment(sketch, "E5.27.9.0", {"start": v(-35.24, -27.77) * mm, "end": v(-27.88, -27.77) * mm});
            skLineSegment(sketch, "E5.30.9.0", {"start": v(27.88, -27.77) * mm, "end": v(35.24, -27.77) * mm});
            skLineSegment(sketch, "E5.33.9.0", {"start": v(-8.2, -35.14) * mm, "end": v(-0.83, -35.14) * mm});
            skLineSegment(sketch, "E5.36.9.0", {"start": v(-35.24, -27.77) * mm, "end": v(-35.24, -35.14) * mm});
            skLineSegment(sketch, "E5.39.9.0", {"start": v(-27.88, -27.77) * mm, "end": v(-27.88, -35.14) * mm});
            skLineSegment(sketch, "E5.42.9.0", {"start": v(0.83, -35.14) * mm, "end": v(8.2, -35.14) * mm});
            skLineSegment(sketch, "E5.45.9.0", {"start": v(18.86, -35.14) * mm, "end": v(26.23, -35.14) * mm});
            skLineSegment(sketch, "E5.48.9.0", {"start": v(-18.86, -27.77) * mm, "end": v(-18.86, -35.14) * mm});
            skLineSegment(sketch, "E5.51.9.0", {"start": v(-26.23, -35.14) * mm, "end": v(-18.86, -35.14) * mm});
            skLineSegment(sketch, "E5.54.9.0", {"start": v(-26.23, -27.77) * mm, "end": v(-26.23, -35.14) * mm});
            skLineSegment(sketch, "E5.57.9.0", {"start": v(-26.23, -27.77) * mm, "end": v(-18.86, -27.77) * mm});
            skLineSegment(sketch, "E5.60.9.0", {"start": v(-9.84, -27.77) * mm, "end": v(-9.84, -35.14) * mm});
            skLineSegment(sketch, "E5.63.9.0", {"start": v(9.84, -27.77) * mm, "end": v(9.84, -35.14) * mm});
            skLineSegment(sketch, "E5.66.9.0", {"start": v(9.84, -27.77) * mm, "end": v(17.2, -27.77) * mm});
            skLineSegment(sketch, "E5.69.9.0", {"start": v(17.2, -27.77) * mm, "end": v(17.2, -35.14) * mm});
            skLineSegment(sketch, "E5.72.9.0", {"start": v(27.88, -35.14) * mm, "end": v(35.24, -35.14) * mm});
            skLineSegment(sketch, "E5.75.9.0", {"start": v(0.83, -27.77) * mm, "end": v(0.83, -35.14) * mm});
            skLineSegment(sketch, "E5.78.9.0", {"start": v(18.86, -27.77) * mm, "end": v(18.86, -35.14) * mm});
            skLineSegment(sketch, "E5.81.9.0", {"start": v(27.88, -27.77) * mm, "end": v(27.88, -35.14) * mm});
            skLineSegment(sketch, "E5.84.9.0", {"start": v(9.84, -35.14) * mm, "end": v(17.2, -35.14) * mm});
            skLineSegment(sketch, "E5.87.9.0", {"start": v(26.23, -27.77) * mm, "end": v(26.23, -35.14) * mm});
            skLineSegment(sketch, "E5.90.9.0", {"start": v(-8.2, -27.77) * mm, "end": v(-8.2, -35.14) * mm});
            skLineSegment(sketch, "E5.93.9.0", {"start": v(35.24, -27.77) * mm, "end": v(35.24, -35.14) * mm});
            skLineSegment(sketch, "E5.0.10.0", {"start": v(-8.2, -36.77) * mm, "end": v(-0.83, -36.77) * mm});
            skLineSegment(sketch, "E5.3.10.0", {"start": v(0.83, -36.77) * mm, "end": v(8.2, -36.77) * mm});
            skLineSegment(sketch, "E5.6.10.0", {"start": v(18.86, -36.77) * mm, "end": v(26.23, -36.77) * mm});
            skLineSegment(sketch, "E5.9.10.0", {"start": v(-17.2, -44.13) * mm, "end": v(-9.84, -44.13) * mm});
            skLineSegment(sketch, "E5.12.10.0", {"start": v(8.2, -36.77) * mm, "end": v(8.2, -44.13) * mm});
            skLineSegment(sketch, "E5.15.10.0", {"start": v(-35.24, -44.13) * mm, "end": v(-27.88, -44.13) * mm});
            skLineSegment(sketch, "E5.18.10.0", {"start": v(-17.2, -36.77) * mm, "end": v(-17.2, -44.13) * mm});
            skLineSegment(sketch, "E5.21.10.0", {"start": v(-17.2, -36.77) * mm, "end": v(-9.84, -36.77) * mm});
            skLineSegment(sketch, "E5.24.10.0", {"start": v(-0.83, -36.77) * mm, "end": v(-0.83, -44.13) * mm});
            skLineSegment(sketch, "E5.27.10.0", {"start": v(-35.24, -36.77) * mm, "end": v(-27.88, -36.77) * mm});
            skLineSegment(sketch, "E5.30.10.0", {"start": v(27.88, -36.77) * mm, "end": v(35.24, -36.77) * mm});
            skLineSegment(sketch, "E5.33.10.0", {"start": v(-8.2, -44.13) * mm, "end": v(-0.83, -44.13) * mm});
            skLineSegment(sketch, "E5.36.10.0", {"start": v(-35.24, -36.77) * mm, "end": v(-35.24, -44.13) * mm});
            skLineSegment(sketch, "E5.39.10.0", {"start": v(-27.88, -36.77) * mm, "end": v(-27.88, -44.13) * mm});
            skLineSegment(sketch, "E5.42.10.0", {"start": v(0.83, -44.13) * mm, "end": v(8.2, -44.13) * mm});
            skLineSegment(sketch, "E5.45.10.0", {"start": v(18.86, -44.13) * mm, "end": v(26.23, -44.13) * mm});
            skLineSegment(sketch, "E5.48.10.0", {"start": v(-18.86, -36.77) * mm, "end": v(-18.86, -44.13) * mm});
            skLineSegment(sketch, "E5.51.10.0", {"start": v(-26.23, -44.13) * mm, "end": v(-18.86, -44.13) * mm});
            skLineSegment(sketch, "E5.54.10.0", {"start": v(-26.23, -36.77) * mm, "end": v(-26.23, -44.13) * mm});
            skLineSegment(sketch, "E5.57.10.0", {"start": v(-26.23, -36.77) * mm, "end": v(-18.86, -36.77) * mm});
            skLineSegment(sketch, "E5.60.10.0", {"start": v(-9.84, -36.77) * mm, "end": v(-9.84, -44.13) * mm});
            skLineSegment(sketch, "E5.63.10.0", {"start": v(9.84, -36.77) * mm, "end": v(9.84, -44.13) * mm});
            skLineSegment(sketch, "E5.66.10.0", {"start": v(9.84, -36.77) * mm, "end": v(17.2, -36.77) * mm});
            skLineSegment(sketch, "E5.69.10.0", {"start": v(17.2, -36.77) * mm, "end": v(17.2, -44.13) * mm});
            skLineSegment(sketch, "E5.72.10.0", {"start": v(27.88, -44.13) * mm, "end": v(35.24, -44.13) * mm});
            skLineSegment(sketch, "E5.75.10.0", {"start": v(0.83, -36.77) * mm, "end": v(0.83, -44.13) * mm});
            skLineSegment(sketch, "E5.78.10.0", {"start": v(18.86, -36.77) * mm, "end": v(18.86, -44.13) * mm});
            skLineSegment(sketch, "E5.81.10.0", {"start": v(27.88, -36.77) * mm, "end": v(27.88, -44.13) * mm});
            skLineSegment(sketch, "E5.84.10.0", {"start": v(9.84, -44.13) * mm, "end": v(17.2, -44.13) * mm});
            skLineSegment(sketch, "E5.87.10.0", {"start": v(26.23, -36.77) * mm, "end": v(26.23, -44.13) * mm});
            skLineSegment(sketch, "E5.90.10.0", {"start": v(-8.2, -36.77) * mm, "end": v(-8.2, -44.13) * mm});
            skLineSegment(sketch, "E5.93.10.0", {"start": v(35.24, -36.77) * mm, "end": v(35.24, -44.13) * mm});
            skLineSegment(sketch, "E5.0.11.0", {"start": v(-8.2, -45.76) * mm, "end": v(-0.83, -45.76) * mm});
            skLineSegment(sketch, "E5.3.11.0", {"start": v(0.83, -45.76) * mm, "end": v(8.2, -45.76) * mm});
            skLineSegment(sketch, "E5.6.11.0", {"start": v(18.86, -45.76) * mm, "end": v(26.23, -45.76) * mm});
            skLineSegment(sketch, "E5.9.11.0", {"start": v(-17.2, -53.12) * mm, "end": v(-9.84, -53.12) * mm});
            skLineSegment(sketch, "E5.12.11.0", {"start": v(8.2, -45.76) * mm, "end": v(8.2, -53.12) * mm});
            skLineSegment(sketch, "E5.15.11.0", {"start": v(-35.24, -53.12) * mm, "end": v(-27.88, -53.12) * mm});
            skLineSegment(sketch, "E5.18.11.0", {"start": v(-17.2, -45.76) * mm, "end": v(-17.2, -53.12) * mm});
            skLineSegment(sketch, "E5.21.11.0", {"start": v(-17.2, -45.76) * mm, "end": v(-9.84, -45.76) * mm});
            skLineSegment(sketch, "E5.24.11.0", {"start": v(-0.83, -45.76) * mm, "end": v(-0.83, -53.12) * mm});
            skLineSegment(sketch, "E5.27.11.0", {"start": v(-35.24, -45.76) * mm, "end": v(-27.88, -45.76) * mm});
            skLineSegment(sketch, "E5.30.11.0", {"start": v(27.88, -45.76) * mm, "end": v(35.24, -45.76) * mm});
            skLineSegment(sketch, "E5.33.11.0", {"start": v(-8.2, -53.12) * mm, "end": v(-0.83, -53.12) * mm});
            skLineSegment(sketch, "E5.36.11.0", {"start": v(-35.24, -45.76) * mm, "end": v(-35.24, -53.12) * mm});
            skLineSegment(sketch, "E5.39.11.0", {"start": v(-27.88, -45.76) * mm, "end": v(-27.88, -53.12) * mm});
            skLineSegment(sketch, "E5.42.11.0", {"start": v(0.83, -53.12) * mm, "end": v(8.2, -53.12) * mm});
            skLineSegment(sketch, "E5.45.11.0", {"start": v(18.86, -53.12) * mm, "end": v(26.23, -53.12) * mm});
            skLineSegment(sketch, "E5.48.11.0", {"start": v(-18.86, -45.76) * mm, "end": v(-18.86, -53.12) * mm});
            skLineSegment(sketch, "E5.51.11.0", {"start": v(-26.23, -53.12) * mm, "end": v(-18.86, -53.12) * mm});
            skLineSegment(sketch, "E5.54.11.0", {"start": v(-26.23, -45.76) * mm, "end": v(-26.23, -53.12) * mm});
            skLineSegment(sketch, "E5.57.11.0", {"start": v(-26.23, -45.76) * mm, "end": v(-18.86, -45.76) * mm});
            skLineSegment(sketch, "E5.60.11.0", {"start": v(-9.84, -45.76) * mm, "end": v(-9.84, -53.12) * mm});
            skLineSegment(sketch, "E5.63.11.0", {"start": v(9.84, -45.76) * mm, "end": v(9.84, -53.12) * mm});
            skLineSegment(sketch, "E5.66.11.0", {"start": v(9.84, -45.76) * mm, "end": v(17.2, -45.76) * mm});
            skLineSegment(sketch, "E5.69.11.0", {"start": v(17.2, -45.76) * mm, "end": v(17.2, -53.12) * mm});
            skLineSegment(sketch, "E5.72.11.0", {"start": v(27.88, -53.12) * mm, "end": v(35.24, -53.12) * mm});
            skLineSegment(sketch, "E5.75.11.0", {"start": v(0.83, -45.76) * mm, "end": v(0.83, -53.12) * mm});
            skLineSegment(sketch, "E5.78.11.0", {"start": v(18.86, -45.76) * mm, "end": v(18.86, -53.12) * mm});
            skLineSegment(sketch, "E5.81.11.0", {"start": v(27.88, -45.76) * mm, "end": v(27.88, -53.12) * mm});
            skLineSegment(sketch, "E5.84.11.0", {"start": v(9.84, -53.12) * mm, "end": v(17.2, -53.12) * mm});
            skLineSegment(sketch, "E5.87.11.0", {"start": v(26.23, -45.76) * mm, "end": v(26.23, -53.12) * mm});
            skLineSegment(sketch, "E5.90.11.0", {"start": v(-8.2, -45.76) * mm, "end": v(-8.2, -53.12) * mm});
            skLineSegment(sketch, "E5.93.11.0", {"start": v(35.24, -45.76) * mm, "end": v(35.24, -53.12) * mm});
            skSolve(sketch);
        }
        {
            var Q0;
            Q0=qSketchRegion(id+"F0",true);
            extrude(context, id + "F1", {"entities" : qUnion([Q0]), "depth" : 0.03 * mm});
        }
    });
